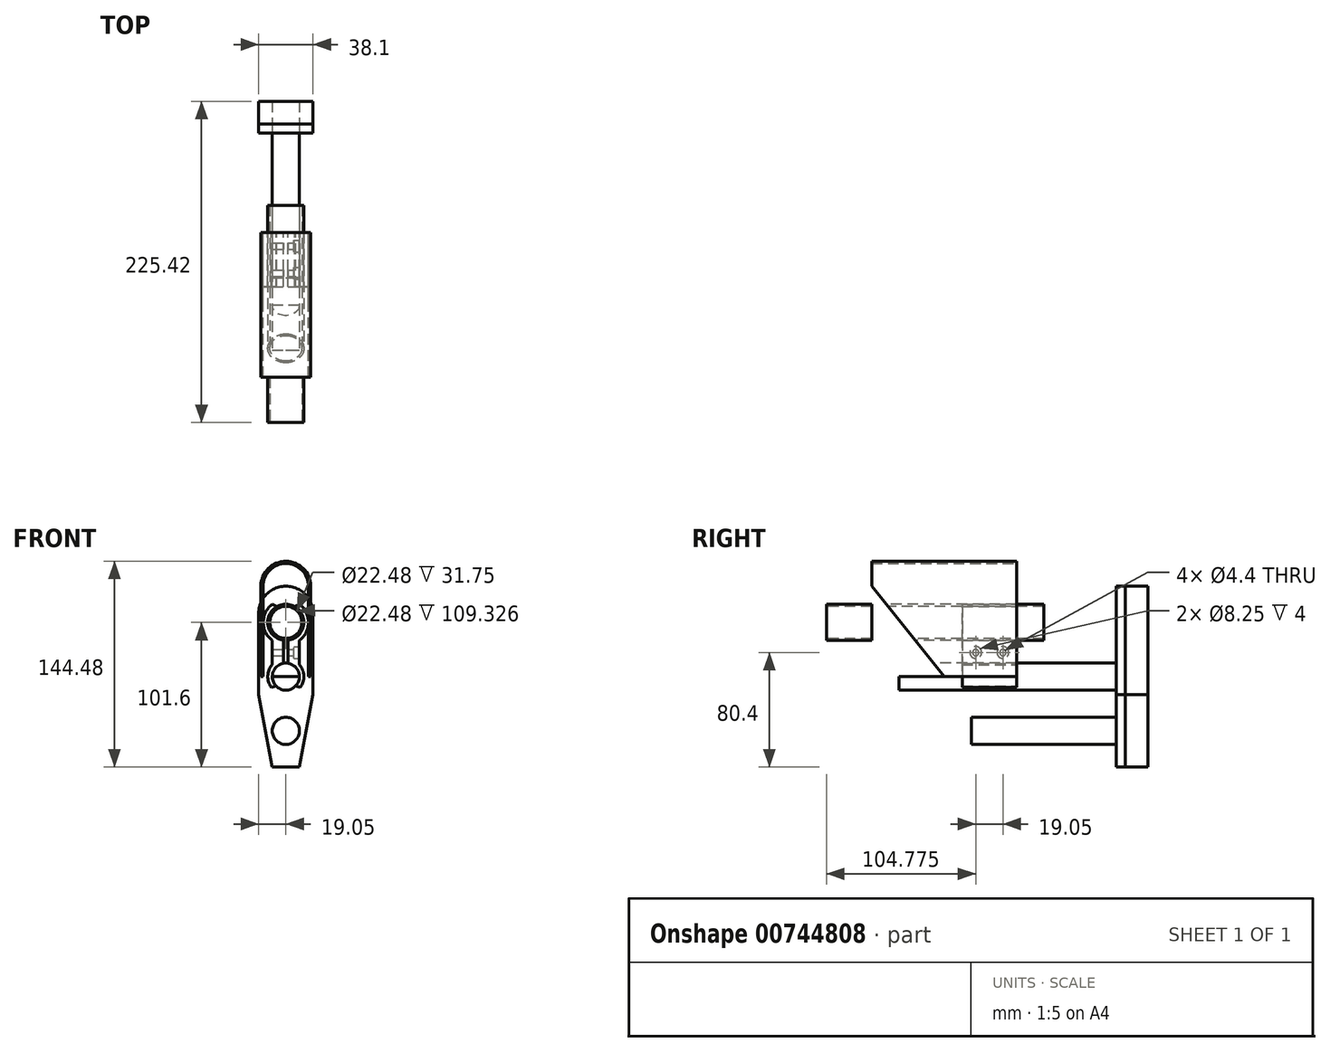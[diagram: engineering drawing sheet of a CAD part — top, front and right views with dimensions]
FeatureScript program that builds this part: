
annotation { "Feature Type Name" : "Feature", "Feature Type Description" : "" }
export const myFeature = defineFeature(function(context is Context, id is Id, definition is map)
    precondition{}
    {
        {
            var Q0;
            Q0=qCreatedBy(makeId("Front.planeOp"),FACE);
            var sketch = newSketch(context, id + "F0", { "sketchPlane" : qUnion([Q0])});
            skCircle(sketch, "E0", {"center": v(0, 0) * mm, "radius": 12.7 * mm});
            skCircle(sketch, "E1", {"center": v(0, 0) * mm, "radius": 11.24 * mm});
            skSolve(sketch);
        }
        {
            var Q0;
            Q0=makeQuery(id+"F0.imprint","IMPRINT",FACE,{"disambiguationData":[TD([[makeQuery(id+"F0.imprint","IMPRINT",EDGE,{"derivedFrom":sQuery(id+"F0.wireOp",EDGE,"E0")}),1.0]])]});
            extrude(context, id + "F1", {"entities" : qUnion([Q0]), "oppositeDirection" : true, "depth" : 152.4 * mm, "offsetDistance" : 25.4 * mm});
        }
        {
            var Q0;
            Q0=qCreatedBy(makeId("Front.planeOp"),FACE);
            var sketch = newSketch(context, id + "F2", { "sketchPlane" : qUnion([Q0])});
            skLineSegment(sketch, "E2", {"start": v(0, 0) * mm, "end": v(0, -12.7) * mm});
            skCircle(sketch, "E3", {"center": v(0, -38.1) * mm, "radius": 9.53 * mm});
            skSolve(sketch);
        }
        {
            var Q0;
            Q0=makeQuery(id+"F2.imprint","IMPRINT",FACE,{"disambiguationData":[TD([[makeQuery(id+"F2.imprint","IMPRINT",EDGE,{"derivedFrom":sQuery(id+"F2.wireOp",EDGE,"E3")}),1.0]])]});
            extrude(context, id + "F3", {"entities" : qUnion([Q0]), "oppositeDirection" : true, "depth" : 254 * mm, "offsetDistance" : 25.4 * mm, "hasSecondDirection" : true, "secondDirectionOppositeDirection" : true, "secondDirectionDepth" : 101.6 * mm});
        }
        {
            var Q0;
            Q0=makeQuery(id+"F1.opExtrude","CAP_FACE",FACE,{"disambiguationData":[OSD([sQuery(id+"F0.wireOp",EDGE,"E0"),sQuery(id+"F0.wireOp",EDGE,"E1")])],"isStart":false});
            var sketch = newSketch(context, id + "F4", { "sketchPlane" : qUnion([Q0])});
            skLineSegment(sketch, "E4", {"start": v(-9.53, -29.7) * mm, "end": v(-9.53, -12.7) * mm});
            skLineSegment(sketch, "E5", {"start": v(9.53, -29.7) * mm, "end": v(9.53, -12.7) * mm});
            skArc(sketch, "E6", {"start": v(-1.55, -28.7) * mm, "mid": v(-9.28, -35.94) * mm, "end": v(-5.54, -45.85) * mm});
            skArc(sketch, "E7", {"start": v(5.54, -45.85) * mm, "mid": v(9.28, -35.94) * mm, "end": v(1.55, -28.7) * mm});
            skArc(sketch, "E8", {"start": v(-9.53, -29.7) * mm, "mid": v(-12.45, -40.6) * mm, "end": v(-5.54, -49.53) * mm});
            skArc(sketch, "E9", {"start": v(5.54, -49.53) * mm, "mid": v(12.45, -40.6) * mm, "end": v(9.53, -29.7) * mm});
            skLineSegment(sketch, "E10", {"start": v(-1.55, -12.6) * mm, "end": v(-1.55, -28.7) * mm});
            skLineSegment(sketch, "E11", {"start": v(1.55, -12.6) * mm, "end": v(1.55, -28.7) * mm});
            skLineSegment(sketch, "E12", {"start": v(-5.54, -45.85) * mm, "end": v(-5.54, -49.53) * mm});
            skLineSegment(sketch, "E13", {"start": v(5.54, -45.85) * mm, "end": v(5.54, -49.53) * mm});
            skLineSegment(sketch, "E14", {"start": v(-5.54, 14.88) * mm, "end": v(-5.54, 11.43) * mm});
            skLineSegment(sketch, "E15", {"start": v(5.54, 14.88) * mm, "end": v(5.54, 11.43) * mm});
            skArc(sketch, "E16", {"start": v(-5.54, 11.43) * mm, "mid": v(-12.53, -2.08) * mm, "end": v(-1.55, -12.6) * mm});
            skArc(sketch, "E17", {"start": v(1.55, -12.6) * mm, "mid": v(12.53, -2.08) * mm, "end": v(5.54, 11.43) * mm});
            skArc(sketch, "E18", {"start": v(-5.54, 14.88) * mm, "mid": v(-15.71, 2.27) * mm, "end": v(-9.52, -12.7) * mm});
            skArc(sketch, "E19", {"start": v(9.53, -12.7) * mm, "mid": v(15.71, 2.27) * mm, "end": v(5.54, 14.88) * mm});
            skSolve(sketch);
        }
        {
            var Q0;
            Q0=makeQuery(id+"F4.imprint","IMPRINT",FACE,{"disambiguationData":[TD([[makeQuery(id+"F4.imprint","IMPRINT",EDGE,{"derivedFrom":sQuery(id+"F4.wireOp",EDGE,"E4")}),-1.0]])]});
            var Q1;
            Q1=makeQuery(id+"F4.imprint","IMPRINT",FACE,{"disambiguationData":[TD([[makeQuery(id+"F4.imprint","IMPRINT",EDGE,{"derivedFrom":sQuery(id+"F4.wireOp",EDGE,"E5")}),1.0]])]});
            extrude(context, id + "F5", {"entities" : qUnion([Q0, Q1]), "oppositeDirection" : true, "depth" : 38.1 * mm, "offsetDistance" : 25.4 * mm});
        }
        {
            var Q0;
            Q0=makeQuery(id+"F5.opExtrude","SWEPT_BODY",BODY,{"disambiguationData":[OSD([sQuery(id+"F4.wireOp",EDGE,"E4"),sQuery(id+"F4.wireOp",EDGE,"E6"),sQuery(id+"F4.wireOp",EDGE,"E8"),sQuery(id+"F4.wireOp",EDGE,"E10"),sQuery(id+"F4.wireOp",EDGE,"E12"),sQuery(id+"F4.wireOp",EDGE,"E14"),sQuery(id+"F4.wireOp",EDGE,"E16"),sQuery(id+"F4.wireOp",EDGE,"E18")])]});
            var Q1;
            Q1=makeQuery(id+"F5.opExtrude","SWEPT_BODY",BODY,{"disambiguationData":[OSD([sQuery(id+"F4.wireOp",EDGE,"E5"),sQuery(id+"F4.wireOp",EDGE,"E7"),sQuery(id+"F4.wireOp",EDGE,"E9"),sQuery(id+"F4.wireOp",EDGE,"E11"),sQuery(id+"F4.wireOp",EDGE,"E13"),sQuery(id+"F4.wireOp",EDGE,"E15"),sQuery(id+"F4.wireOp",EDGE,"E17"),sQuery(id+"F4.wireOp",EDGE,"E19")])]});
            transform(context, id + "F6", {"entities" : qUnion([Q0, Q1]), "transformType" : TransformType.TRANSLATION_3D, "dx" : 0 * mm, "dy" : -38.1 * mm, "dz" : 0 * mm, "makeCopy" : false});
        }
        {
            var Q0;
            Q0=makeQuery(id+"F3.opExtrude","SWEPT_BODY",BODY,{"disambiguationData":[OSD([sQuery(id+"F2.wireOp",EDGE,"E3"),sQuery(id+"F2.wireOp",EDGE,"uk8BEfQW-RL3J-Y91h-f3YM-nyCw2dlJ58PM")])]});
            transform(context, id + "F7", {"entities" : qUnion([Q0]), "transformType" : TransformType.TRANSLATION_3D, "dx" : 0 * mm, "dy" : 0 * mm, "dz" : -25.4 * mm, "makeCopy" : true});
        }
        {
            var Q0;
            Q0=makeQuery(id+"F3.opExtrude","CAP_FACE",FACE,{"disambiguationData":[OSD([sQuery(id+"F2.wireOp",EDGE,"E3"),sQuery(id+"F2.wireOp",EDGE,"uk8BEfQW-RL3J-Y91h-f3YM-nyCw2dlJ58PM")])],"isStart":false});
            var sketch = newSketch(context, id + "F8", { "sketchPlane" : qUnion([Q0])});
            skArc(sketch, "E20", {"start": v(19.05, -6.35) * mm, "mid": v(0, 12.7) * mm, "end": v(-19.05, -6.35) * mm});
            skLineSegment(sketch, "E21", {"start": v(-19.05, -38.1) * mm, "end": v(-19.05, -63.5) * mm});
            skLineSegment(sketch, "E22", {"start": v(-19.05, -6.35) * mm, "end": v(-19.05, -38.1) * mm});
            skLineSegment(sketch, "E23", {"start": v(19.05, -6.35) * mm, "end": v(19.05, -38.1) * mm});
            skLineSegment(sketch, "E24", {"start": v(19.05, -38.1) * mm, "end": v(19.05, -63.5) * mm});
            skLineSegment(sketch, "E25", {"start": v(0, -114.3) * mm, "end": v(9.53, -114.3) * mm});
            skLineSegment(sketch, "E26", {"start": v(0, -114.3) * mm, "end": v(-9.53, -114.3) * mm});
            skLineSegment(sketch, "E27", {"start": v(-19.05, -63.5) * mm, "end": v(-9.52, -114.3) * mm});
            skLineSegment(sketch, "E28", {"start": v(19.05, -63.5) * mm, "end": v(9.52, -114.3) * mm});
            skSolve(sketch);
        }
        {
            var Q0;
            Q0=makeQuery(id+"F8.imprint","IMPRINT",FACE,{"disambiguationData":[TD([[makeQuery(id+"F8.imprint","IMPRINT",EDGE,{"derivedFrom":sQuery(id+"F8.wireOp",EDGE,"MivVW0rG-suHv-gdVa-b4fH-uG9gUaePJ1Vy")}),1.0]])]});
            var Q1;
            Q1=makeQuery(id+"F8.imprint","IMPRINT",FACE,{"disambiguationData":[TD([[makeQuery(id+"F8.imprint","IMPRINT",EDGE,{"derivedFrom":sQuery(id+"F8.wireOp",EDGE,"E20")}),1.0]])]});
            var Q2;
            Q2=makeQuery(id+"F8.imprint","IMPRINT",FACE,{"disambiguationData":[TD([[makeQuery(id+"F8.imprint","IMPRINT",EDGE,{"derivedFrom":makeQuery(id+"F3.opExtrude","CAP_EDGE",EDGE,{"disambiguationData":[OSD([sQuery(id+"F2.wireOp",EDGE,"E3")])],"isStart":false})}),-1.0]])]});
            extrude(context, id + "F9", {"entities" : qUnion([Q0, Q1, Q2]), "depth" : 6.35 * mm, "offsetDistance" : 25.4 * mm});
        }
        {
            var Q0;
            Q0=makeQuery(id+"F5.opExtrude","SWEPT_FACE",FACE,{"disambiguationData":[OSD([sQuery(id+"F4.wireOp",EDGE,"E4")])]});
            var sketch = newSketch(context, id + "F10", { "sketchPlane" : qUnion([Q0])});
            skLineSegment(sketch, "E29", {"start": v(76.2, -21.2) * mm, "end": v(85.73, -21.2) * mm});
            skLineSegment(sketch, "E30", {"start": v(114.3, -21.2) * mm, "end": v(104.78, -21.2) * mm});
            skSolve(sketch);
        }
        {
            var Q0;
            Q0=sQuery(id+"F10.wireOp",VERTEX,"E29.end");
            var Q1;
            Q1=sQuery(id+"F10.wireOp",VERTEX,"E30.end");
            var Q2;
            Q2=makeQuery(id+"F5.opExtrude","SWEPT_BODY",BODY,{"disambiguationData":[OSD([sQuery(id+"F4.wireOp",EDGE,"E4"),sQuery(id+"F4.wireOp",EDGE,"E6"),sQuery(id+"F4.wireOp",EDGE,"E8"),sQuery(id+"F4.wireOp",EDGE,"E10"),sQuery(id+"F4.wireOp",EDGE,"E12"),sQuery(id+"F4.wireOp",EDGE,"E14"),sQuery(id+"F4.wireOp",EDGE,"E16"),sQuery(id+"F4.wireOp",EDGE,"E18")])]});
            var Q3;
            Q3=makeQuery(id+"F5.opExtrude","SWEPT_BODY",BODY,{"disambiguationData":[OSD([sQuery(id+"F4.wireOp",EDGE,"E5"),sQuery(id+"F4.wireOp",EDGE,"E7"),sQuery(id+"F4.wireOp",EDGE,"E9"),sQuery(id+"F4.wireOp",EDGE,"E11"),sQuery(id+"F4.wireOp",EDGE,"E13"),sQuery(id+"F4.wireOp",EDGE,"E15"),sQuery(id+"F4.wireOp",EDGE,"E17"),sQuery(id+"F4.wireOp",EDGE,"E19")])]});
            hole(context, id + "F11", {"style" : HoleStyle.C_BORE, "endStyle" : HoleEndStyle.THROUGH, "standardTappedOrClearance" : lookupTablePath({ "fit" : "Normal", "standard" : "ISO", "size" : "M4", "type" : "Clearance" }), "standardBlindInLast" : lookupTablePath({ "fit" : "Standard", "standard" : "ISO", "size" : "M4", "type" : "Clearance" }), "holeDiameter" : 4.4 * mm, "cBoreDiameter" : 8.25 * mm, "cBoreDepth" : 4 * mm, "majorDiameter" : 4 * mm, "isTappedThrough" : true, "tappedDepth" : 6.34 * mm, "tapClearance" : 3, "locations" : qUnion([Q0, Q1]), "scope" : qUnion([Q2, Q3])});
        }
        {
            var Q0;
            Q0=makeQuery(id+"F5.opExtrude","SWEPT_EDGE",EDGE,{"disambiguationData":[OSD([sQuery(id+"F4.wireOp",EDGE,"E9"),sQuery(id+"F4.wireOp",EDGE,"E13")])]});
            var Q1;
            Q1=makeQuery(id+"F5.opExtrude","SWEPT_EDGE",EDGE,{"disambiguationData":[OSD([sQuery(id+"F4.wireOp",EDGE,"E8"),sQuery(id+"F4.wireOp",EDGE,"E12")])]});
            var Q2;
            Q2=makeQuery(id+"F5.opExtrude","SWEPT_EDGE",EDGE,{"disambiguationData":[OSD([sQuery(id+"F4.wireOp",EDGE,"E14"),sQuery(id+"F4.wireOp",EDGE,"E18")])]});
            var Q3;
            Q3=makeQuery(id+"F5.opExtrude","SWEPT_EDGE",EDGE,{"disambiguationData":[OSD([sQuery(id+"F4.wireOp",EDGE,"E15"),sQuery(id+"F4.wireOp",EDGE,"E19")])]});
            chamfer(context, id + "F12", {"entities" : qUnion([Q0, Q1, Q2, Q3]), "width" : 2.54 * mm, "tangentPropagation" : true});
        }
        {
            var Q0;
            Q0=makeQuery(id+"F9.opExtrude","SWEPT_BODY",BODY,{"disambiguationData":[OSD([sQuery(id+"F8.wireOp",EDGE,"E20"),sQuery(id+"F8.wireOp",EDGE,"E21"),sQuery(id+"F8.wireOp",EDGE,"E22"),sQuery(id+"F8.wireOp",EDGE,"E23"),sQuery(id+"F8.wireOp",EDGE,"E24"),sQuery(id+"F8.wireOp",EDGE,"E25"),sQuery(id+"F8.wireOp",EDGE,"E26"),sQuery(id+"F8.wireOp",EDGE,"E27"),sQuery(id+"F8.wireOp",EDGE,"E28")])]});
            transform(context, id + "F13", {"entities" : qUnion([Q0]), "transformType" : TransformType.TRANSLATION_3D, "dx" : 0 * mm, "dy" : 0 * mm, "dz" : 12.7 * mm, "makeCopy" : false});
        }
        {
            var Q0;
            Q0=makeQuery(id+"F9.opExtrude","SWEPT_BODY",BODY,{"disambiguationData":[OSD([sQuery(id+"F8.wireOp",EDGE,"E20"),sQuery(id+"F8.wireOp",EDGE,"E21"),sQuery(id+"F8.wireOp",EDGE,"E22"),sQuery(id+"F8.wireOp",EDGE,"E23"),sQuery(id+"F8.wireOp",EDGE,"E24"),sQuery(id+"F8.wireOp",EDGE,"E25"),sQuery(id+"F8.wireOp",EDGE,"E26"),sQuery(id+"F8.wireOp",EDGE,"E27"),sQuery(id+"F8.wireOp",EDGE,"E28")])]});
            transform(context, id + "F14", {"entities" : qUnion([Q0]), "transformType" : TransformType.TRANSLATION_3D, "dx" : 0 * mm, "dy" : 6.35 * mm, "dz" : 0 * mm, "makeCopy" : true});
        }
        {
            var Q0;
            Q0=makeQuery(id+"F14.opPattern","COPY",FACE,{"derivedFrom":makeQuery(id+"F9.opExtrude","CAP_FACE",FACE,{"disambiguationData":[OSD([sQuery(id+"F8.wireOp",EDGE,"E20"),sQuery(id+"F8.wireOp",EDGE,"E21"),sQuery(id+"F8.wireOp",EDGE,"E22"),sQuery(id+"F8.wireOp",EDGE,"E23"),sQuery(id+"F8.wireOp",EDGE,"E24"),sQuery(id+"F8.wireOp",EDGE,"E25"),sQuery(id+"F8.wireOp",EDGE,"E26"),sQuery(id+"F8.wireOp",EDGE,"E27"),sQuery(id+"F8.wireOp",EDGE,"E28")])],"isStart":false}),"instanceName":"1"});
            extrude(context, id + "F15", {"entities" : qUnion([Q0]), "operationType" : NewBodyOperationType.ADD, "depth" : 9.52 * mm, "offsetDistance" : 25.4 * mm});
        }
        {
            var Q0;
            Q0=makeQuery(id+"F5.opExtrude","SWEPT_BODY",BODY,{"disambiguationData":[OSD([sQuery(id+"F4.wireOp",EDGE,"E4"),sQuery(id+"F4.wireOp",EDGE,"E6"),sQuery(id+"F4.wireOp",EDGE,"E8"),sQuery(id+"F4.wireOp",EDGE,"E10"),sQuery(id+"F4.wireOp",EDGE,"E12"),sQuery(id+"F4.wireOp",EDGE,"E14"),sQuery(id+"F4.wireOp",EDGE,"E16"),sQuery(id+"F4.wireOp",EDGE,"E18")])]});
            var Q1;
            Q1=makeQuery(id+"F5.opExtrude","SWEPT_BODY",BODY,{"disambiguationData":[OSD([sQuery(id+"F4.wireOp",EDGE,"E5"),sQuery(id+"F4.wireOp",EDGE,"E7"),sQuery(id+"F4.wireOp",EDGE,"E9"),sQuery(id+"F4.wireOp",EDGE,"E11"),sQuery(id+"F4.wireOp",EDGE,"E13"),sQuery(id+"F4.wireOp",EDGE,"E15"),sQuery(id+"F4.wireOp",EDGE,"E17"),sQuery(id+"F4.wireOp",EDGE,"E19")])]});
            transform(context, id + "F16", {"entities" : qUnion([Q0, Q1]), "transformType" : TransformType.TRANSLATION_3D, "dx" : 0 * mm, "dy" : 19.05 * mm, "dz" : 0 * mm, "makeCopy" : false});
        }
        {
            var Q0;
            Q0=makeQuery(id+"F3.opExtrude","SWEPT_BODY",BODY,{"disambiguationData":[OSD([sQuery(id+"F2.wireOp",EDGE,"E3")])]});
            var Q1;
            Q1=makeQuery(id+"F9.opExtrude","SWEPT_BODY",BODY,{"disambiguationData":[OSD([sQuery(id+"F8.wireOp",EDGE,"E20"),sQuery(id+"F8.wireOp",EDGE,"E21"),sQuery(id+"F8.wireOp",EDGE,"E22"),sQuery(id+"F8.wireOp",EDGE,"E23"),sQuery(id+"F8.wireOp",EDGE,"E24"),sQuery(id+"F8.wireOp",EDGE,"E25"),sQuery(id+"F8.wireOp",EDGE,"E26"),sQuery(id+"F8.wireOp",EDGE,"E27"),sQuery(id+"F8.wireOp",EDGE,"E28")])]});
            var Q2;
            Q2=makeQuery(id+"F14.opPattern","COPY",BODY,{"derivedFrom":makeQuery(id+"F9.opExtrude","SWEPT_BODY",BODY,{"disambiguationData":[OSD([sQuery(id+"F8.wireOp",EDGE,"E20"),sQuery(id+"F8.wireOp",EDGE,"E21"),sQuery(id+"F8.wireOp",EDGE,"E22"),sQuery(id+"F8.wireOp",EDGE,"E23"),sQuery(id+"F8.wireOp",EDGE,"E24"),sQuery(id+"F8.wireOp",EDGE,"E25"),sQuery(id+"F8.wireOp",EDGE,"E26"),sQuery(id+"F8.wireOp",EDGE,"E27"),sQuery(id+"F8.wireOp",EDGE,"E28")])]}),"instanceName":"1"});
            var Q3;
            Q3=makeQuery(id+"F7.opPattern","COPY",BODY,{"derivedFrom":makeQuery(id+"F3.opExtrude","SWEPT_BODY",BODY,{"disambiguationData":[OSD([sQuery(id+"F2.wireOp",EDGE,"E3")])]}),"instanceName":"1"});
            transform(context, id + "F17", {"entities" : qUnion([Q0, Q1, Q2, Q3]), "transformType" : TransformType.TRANSLATION_3D, "dx" : 0 * mm, "dy" : -50.8 * mm, "dz" : 0 * mm, "makeCopy" : false});
        }
        {
            var Q0;
            Q0=makeQuery(id+"F7.opPattern","COPY",BODY,{"derivedFrom":makeQuery(id+"F3.opExtrude","SWEPT_BODY",BODY,{"disambiguationData":[OSD([sQuery(id+"F2.wireOp",EDGE,"E3")])]}),"instanceName":"1"});
            transform(context, id + "F18", {"entities" : qUnion([Q0]), "transformType" : TransformType.TRANSLATION_3D, "dx" : 0 * mm, "dy" : 0 * mm, "dz" : -12.7 * mm, "makeCopy" : false});
        }
        {
            var Q0;
            Q0=makeQuery(id+"F7.opPattern","COPY",FACE,{"derivedFrom":makeQuery(id+"F3.opExtrude","CAP_FACE",FACE,{"disambiguationData":[OSD([sQuery(id+"F2.wireOp",EDGE,"E3")])],"isStart":true}),"instanceName":"1"});
            extrude(context, id + "F19", {"entities" : qUnion([Q0]), "operationType" : NewBodyOperationType.REMOVE, "oppositeDirection" : true, "depth" : 50.8 * mm, "offsetDistance" : 25.4 * mm});
        }
        {
            var Q0;
            Q0=makeQuery(id+"F5.opExtrude","CAP_FACE",FACE,{"disambiguationData":[OSD([sQuery(id+"F4.wireOp",EDGE,"E5"),sQuery(id+"F4.wireOp",EDGE,"E7"),sQuery(id+"F4.wireOp",EDGE,"E9"),sQuery(id+"F4.wireOp",EDGE,"E11"),sQuery(id+"F4.wireOp",EDGE,"E13"),sQuery(id+"F4.wireOp",EDGE,"E15"),sQuery(id+"F4.wireOp",EDGE,"E17"),sQuery(id+"F4.wireOp",EDGE,"E19")])],"isStart":true});
            var sketch = newSketch(context, id + "F20", { "sketchPlane" : qUnion([Q0])});
            skLineSegment(sketch, "E31", {"start": v(-15.88, 0) * mm, "end": v(-15.88, -63.5) * mm});
            skLineSegment(sketch, "E32", {"start": v(15.88, 0) * mm, "end": v(15.88, -63.5) * mm});
            skLineSegment(sketch, "E33", {"start": v(15.88, -63.5) * mm, "end": v(17.48, -63.5) * mm});
            skLineSegment(sketch, "E34", {"start": v(-15.88, -63.5) * mm, "end": v(-17.48, -63.5) * mm});
            skLineSegment(sketch, "E35", {"start": v(-17.48, -63.5) * mm, "end": v(-17.48, 0) * mm});
            skLineSegment(sketch, "E36", {"start": v(17.48, -63.5) * mm, "end": v(17.48, 0) * mm});
            skArc(sketch, "E37", {"start": v(17.48, 0) * mm, "mid": v(0, 17.48) * mm, "end": v(-17.48, 0) * mm});
            skArc(sketch, "E38", {"start": v(15.88, 0) * mm, "mid": v(0, 15.88) * mm, "end": v(-15.88, 0) * mm});
            skSolve(sketch);
        }
        {
            var Q0;
            {var subQ1=sQuery(id+"F20.wireOp",EDGE,"E31");Q0=makeQuery(id+"F20.imprint","IMPRINT",FACE,{"disambiguationData":[TD([[makeQuery(id+"F20.imprint","IMPRINT",EDGE,{"derivedFrom":subQ1}),-1.0]])]});}
            extrude(context, id + "F21", {"entities" : qUnion([Q0]), "oppositeDirection" : true, "depth" : 101.6 * mm, "offsetDistance" : 25.4 * mm});
        }
        {
            var Q0;
            Q0=makeQuery(id+"F21.opExtrude","SWEPT_BODY",BODY,{"disambiguationData":[OSD([sQuery(id+"F20.wireOp",EDGE,"E31"),sQuery(id+"F20.wireOp",EDGE,"E32"),sQuery(id+"F20.wireOp",EDGE,"E33"),sQuery(id+"F20.wireOp",EDGE,"E34"),sQuery(id+"F20.wireOp",EDGE,"E35"),sQuery(id+"F20.wireOp",EDGE,"E36"),sQuery(id+"F20.wireOp",EDGE,"E37"),sQuery(id+"F20.wireOp",EDGE,"E38")])]});
            transform(context, id + "F22", {"entities" : qUnion([Q0]), "transformType" : TransformType.TRANSLATION_3D, "dx" : 0 * mm, "dy" : 0 * mm, "dz" : 25.4 * mm, "makeCopy" : false});
        }
        {
            var Q0;
            Q0=makeQuery(id+"F21.opExtrude","SWEPT_FACE",FACE,{"disambiguationData":[OSD([sQuery(id+"F20.wireOp",EDGE,"E35")])]});
            var sketch = newSketch(context, id + "F23", { "sketchPlane" : qUnion([Q0])});
            skLineSegment(sketch, "E39", {"start": v(31.75, 25.4) * mm, "end": v(82.55, -38.1) * mm});
            skSolve(sketch);
        }
        {
            var Q0;
            {var subQ0=sQuery(id+"F23.wireOp",EDGE,"E39");Q0=makeQuery(id+"F23.imprint","IMPRINT",FACE,{"disambiguationData":[TD([[makeQuery(id+"F23.imprint","IMPRINT",EDGE,{"derivedFrom":subQ0}),-1.0]])]});}
            extrude(context, id + "F24", {"entities" : qUnion([Q0]), "operationType" : NewBodyOperationType.REMOVE, "endBound" : BoundingType.THROUGH_ALL, "oppositeDirection" : true, "depth" : 25.4 * mm, "offsetDistance" : 25.4 * mm});
        }
    });
